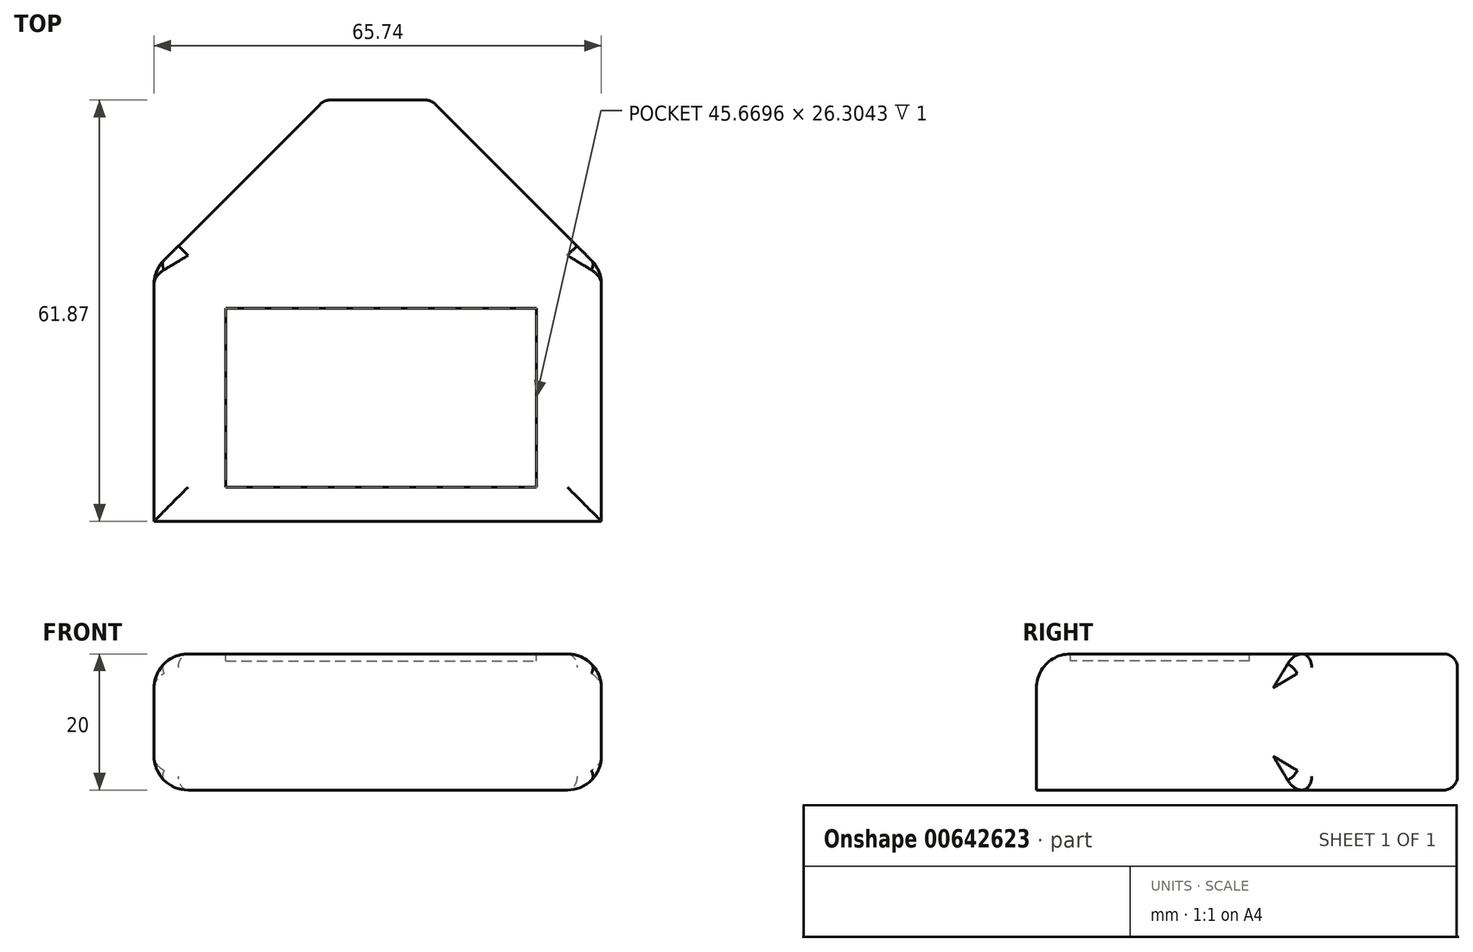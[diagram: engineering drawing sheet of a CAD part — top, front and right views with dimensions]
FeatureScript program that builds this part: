
annotation { "Feature Type Name" : "Feature", "Feature Type Description" : "" }
export const myFeature = defineFeature(function(context is Context, id is Id, definition is map)
    precondition{}
    {
        {
            var Q0;
            Q0=qCreatedBy(makeId("Top.planeOp"),FACE);
            var sketch = newSketch(context, id + "F0", { "sketchPlane" : qUnion([Q0])});
            skLineSegment(sketch, "E0.bottom", {"start": v(-33.05, 30.57) * mm, "end": v(32.69, 30.57) * mm});
            skLineSegment(sketch, "E0.top", {"start": v(-33.05, -31.3) * mm, "end": v(32.69, -31.3) * mm});
            skLineSegment(sketch, "E0.left", {"start": v(-33.05, 30.57) * mm, "end": v(-33.05, -31.3) * mm});
            skLineSegment(sketch, "E0.right", {"start": v(32.69, 30.57) * mm, "end": v(32.69, -31.3) * mm});
            skSolve(sketch);
        }
        {
            var Q0;
            Q0=makeQuery(id+"F0.imprint","IMPRINT",FACE,{"disambiguationData":[TD([[makeQuery(id+"F0.imprint","IMPRINT",EDGE,{"derivedFrom":sQuery(id+"F0.wireOp",EDGE,"E0.bottom")}),-1.0]])]});
            extrude(context, id + "F1", {"entities" : qUnion([Q0]), "depth" : 20 * mm, "offsetDistance" : 25 * mm});
        }
        {
            var Q0;
            Q0=makeQuery(id+"F1.opExtrude","SWEPT_EDGE",EDGE,{"disambiguationData":[OSD([sQuery(id+"F0.wireOp",EDGE,"E0.bottom"),sQuery(id+"F0.wireOp",EDGE,"E0.right")])]});
            chamfer(context, id + "F2", {"entities" : qUnion([Q0]), "width" : 25 * mm, "tangentPropagation" : true});
        }
        {
            var Q0;
            Q0=makeQuery(id+"F1.opExtrude","SWEPT_EDGE",EDGE,{"disambiguationData":[OSD([sQuery(id+"F0.wireOp",EDGE,"E0.bottom"),sQuery(id+"F0.wireOp",EDGE,"E0.left")])]});
            chamfer(context, id + "F3", {"entities" : qUnion([Q0]), "width" : 25 * mm, "tangentPropagation" : true});
        }
        {
            var Q0;
            {var subQ0=sQuery(id+"F0.wireOp",EDGE,"E0.left");var subQ1=sQuery(id+"F0.wireOp",EDGE,"E0.bottom");Q0=makeQuery(id+"F3.opChamfer","BLEND_EDGE",EDGE,{"blendedFrom":[makeQuery(id+"F1.opExtrude","SWEPT_EDGE",EDGE,{"disambiguationData":[OSD([subQ1,subQ0])]}),makeQuery(id+"F1.opExtrude","CAP_FACE",FACE,{"disambiguationData":[OSD([subQ1,sQuery(id+"F0.wireOp",EDGE,"E0.top"),subQ0,sQuery(id+"F0.wireOp",EDGE,"E0.right")])],"isStart":false})],"blendedInto":[makeQuery(id+"F1.opExtrude","CAP_FACE",FACE,{"disambiguationData":[OSD([subQ1,sQuery(id+"F0.wireOp",EDGE,"E0.top"),subQ0,sQuery(id+"F0.wireOp",EDGE,"E0.right")])],"isStart":false})]});}
            var Q1;
            {var subQ0=sQuery(id+"F0.wireOp",EDGE,"E0.left");var subQ1=sQuery(id+"F0.wireOp",EDGE,"E0.bottom");Q1=makeQuery(id+"F3.opChamfer","BLEND_EDGE",EDGE,{"blendedFrom":[makeQuery(id+"F1.opExtrude","SWEPT_EDGE",EDGE,{"disambiguationData":[OSD([subQ1,subQ0])]}),makeQuery(id+"F1.opExtrude","CAP_FACE",FACE,{"disambiguationData":[OSD([subQ1,sQuery(id+"F0.wireOp",EDGE,"E0.top"),subQ0,sQuery(id+"F0.wireOp",EDGE,"E0.right")])],"isStart":true})],"blendedInto":[makeQuery(id+"F1.opExtrude","CAP_FACE",FACE,{"disambiguationData":[OSD([subQ1,sQuery(id+"F0.wireOp",EDGE,"E0.top"),subQ0,sQuery(id+"F0.wireOp",EDGE,"E0.right")])],"isStart":true})]});}
            var Q2;
            Q2=makeQuery(id+"F1.opExtrude","CAP_EDGE",EDGE,{"disambiguationData":[OSD([sQuery(id+"F0.wireOp",EDGE,"E0.bottom")])],"isStart":false});
            var Q3;
            {var subQ0=sQuery(id+"F0.wireOp",EDGE,"E0.bottom");Q3=makeQuery(id+"F3.opChamfer","BLEND_EDGE",EDGE,{"blendedFrom":[makeQuery(id+"F1.opExtrude","SWEPT_EDGE",EDGE,{"disambiguationData":[OSD([subQ0,sQuery(id+"F0.wireOp",EDGE,"E0.left")])]}),makeQuery(id+"F1.opExtrude","SWEPT_FACE",FACE,{"disambiguationData":[OSD([subQ0])]})],"blendedInto":[makeQuery(id+"F1.opExtrude","SWEPT_FACE",FACE,{"disambiguationData":[OSD([subQ0])]})]});}
            var Q4;
            {var subQ0=sQuery(id+"F0.wireOp",EDGE,"E0.bottom");Q4=makeQuery(id+"F2.opChamfer","BLEND_EDGE",EDGE,{"blendedFrom":[makeQuery(id+"F1.opExtrude","SWEPT_EDGE",EDGE,{"disambiguationData":[OSD([subQ0,sQuery(id+"F0.wireOp",EDGE,"E0.right")])]}),makeQuery(id+"F1.opExtrude","SWEPT_FACE",FACE,{"disambiguationData":[OSD([subQ0])]})],"blendedInto":[makeQuery(id+"F1.opExtrude","SWEPT_FACE",FACE,{"disambiguationData":[OSD([subQ0])]})]});}
            var Q5;
            Q5=makeQuery(id+"F1.opExtrude","CAP_EDGE",EDGE,{"disambiguationData":[OSD([sQuery(id+"F0.wireOp",EDGE,"E0.bottom")])],"isStart":true});
            var Q6;
            {var subQ0=sQuery(id+"F0.wireOp",EDGE,"E0.right");var subQ1=sQuery(id+"F0.wireOp",EDGE,"E0.bottom");Q6=makeQuery(id+"F2.opChamfer","BLEND_EDGE",EDGE,{"blendedFrom":[makeQuery(id+"F1.opExtrude","SWEPT_EDGE",EDGE,{"disambiguationData":[OSD([subQ1,subQ0])]}),makeQuery(id+"F1.opExtrude","CAP_FACE",FACE,{"disambiguationData":[OSD([subQ1,sQuery(id+"F0.wireOp",EDGE,"E0.top"),sQuery(id+"F0.wireOp",EDGE,"E0.left"),subQ0])],"isStart":true})],"blendedInto":[makeQuery(id+"F1.opExtrude","CAP_FACE",FACE,{"disambiguationData":[OSD([subQ1,sQuery(id+"F0.wireOp",EDGE,"E0.top"),sQuery(id+"F0.wireOp",EDGE,"E0.left"),subQ0])],"isStart":true})]});}
            var Q7;
            {var subQ0=sQuery(id+"F0.wireOp",EDGE,"E0.right");var subQ1=sQuery(id+"F0.wireOp",EDGE,"E0.bottom");Q7=makeQuery(id+"F2.opChamfer","BLEND_EDGE",EDGE,{"blendedFrom":[makeQuery(id+"F1.opExtrude","SWEPT_EDGE",EDGE,{"disambiguationData":[OSD([subQ1,subQ0])]}),makeQuery(id+"F1.opExtrude","CAP_FACE",FACE,{"disambiguationData":[OSD([subQ1,sQuery(id+"F0.wireOp",EDGE,"E0.top"),sQuery(id+"F0.wireOp",EDGE,"E0.left"),subQ0])],"isStart":false})],"blendedInto":[makeQuery(id+"F1.opExtrude","CAP_FACE",FACE,{"disambiguationData":[OSD([subQ1,sQuery(id+"F0.wireOp",EDGE,"E0.top"),sQuery(id+"F0.wireOp",EDGE,"E0.left"),subQ0])],"isStart":false})]});}
            fillet(context, id + "F4", {"entities" : qUnion([Q0, Q1, Q2, Q3, Q4, Q5, Q6, Q7]), "radius" : 2 * mm, "tangentPropagation" : true, "allowEdgeOverflow" : false});
        }
        {
            var Q0;
            {var subQ0=sQuery(id+"F0.wireOp",EDGE,"E0.left");Q0=makeQuery(id+"F3.opChamfer","BLEND_EDGE",EDGE,{"blendedFrom":[makeQuery(id+"F1.opExtrude","SWEPT_EDGE",EDGE,{"disambiguationData":[OSD([sQuery(id+"F0.wireOp",EDGE,"E0.bottom"),subQ0])]}),makeQuery(id+"F1.opExtrude","SWEPT_FACE",FACE,{"disambiguationData":[OSD([subQ0])]})],"blendedInto":[makeQuery(id+"F1.opExtrude","SWEPT_FACE",FACE,{"disambiguationData":[OSD([subQ0])]})]});}
            var Q1;
            {var subQ0=sQuery(id+"F0.wireOp",EDGE,"E0.right");Q1=makeQuery(id+"F2.opChamfer","BLEND_EDGE",EDGE,{"blendedFrom":[makeQuery(id+"F1.opExtrude","SWEPT_EDGE",EDGE,{"disambiguationData":[OSD([sQuery(id+"F0.wireOp",EDGE,"E0.bottom"),subQ0])]}),makeQuery(id+"F1.opExtrude","SWEPT_FACE",FACE,{"disambiguationData":[OSD([subQ0])]})],"blendedInto":[makeQuery(id+"F1.opExtrude","SWEPT_FACE",FACE,{"disambiguationData":[OSD([subQ0])]})]});}
            var Q2;
            Q2=makeQuery(id+"F1.opExtrude","CAP_EDGE",EDGE,{"disambiguationData":[OSD([sQuery(id+"F0.wireOp",EDGE,"E0.top")])],"isStart":false});
            fillet(context, id + "F5", {"entities" : qUnion([Q0, Q1, Q2]), "radius" : 5 * mm, "tangentPropagation" : true, "allowEdgeOverflow" : false});
        }
        {
            var Q0;
            Q0=makeQuery(id+"F1.opExtrude","CAP_FACE",FACE,{"disambiguationData":[OSD([sQuery(id+"F0.wireOp",EDGE,"E0.bottom"),sQuery(id+"F0.wireOp",EDGE,"E0.top"),sQuery(id+"F0.wireOp",EDGE,"E0.left"),sQuery(id+"F0.wireOp",EDGE,"E0.right")])],"isStart":false});
            var sketch = newSketch(context, id + "F6", { "sketchPlane" : qUnion([Q0])});
            skLineSegment(sketch, "E1.bottom", {"start": v(-22.52, 0) * mm, "end": v(23.15, 0) * mm});
            skLineSegment(sketch, "E1.top", {"start": v(-22.52, -26.3) * mm, "end": v(23.15, -26.3) * mm});
            skLineSegment(sketch, "E1.left", {"start": v(-22.52, 0) * mm, "end": v(-22.52, -26.3) * mm});
            skLineSegment(sketch, "E1.right", {"start": v(23.15, 0) * mm, "end": v(23.15, -26.3) * mm});
            skSolve(sketch);
        }
        {
            var Q0;
            Q0=makeQuery(id+"F6.imprint","IMPRINT",FACE,{"disambiguationData":[TD([[makeQuery(id+"F6.imprint","IMPRINT",EDGE,{"derivedFrom":sQuery(id+"F6.wireOp",EDGE,"E1.bottom")}),-1.0]])]});
            extrude(context, id + "F7", {"entities" : qUnion([Q0]), "operationType" : NewBodyOperationType.REMOVE, "oppositeDirection" : true, "depth" : 1 * mm, "offsetDistance" : 25 * mm});
        }
    });
